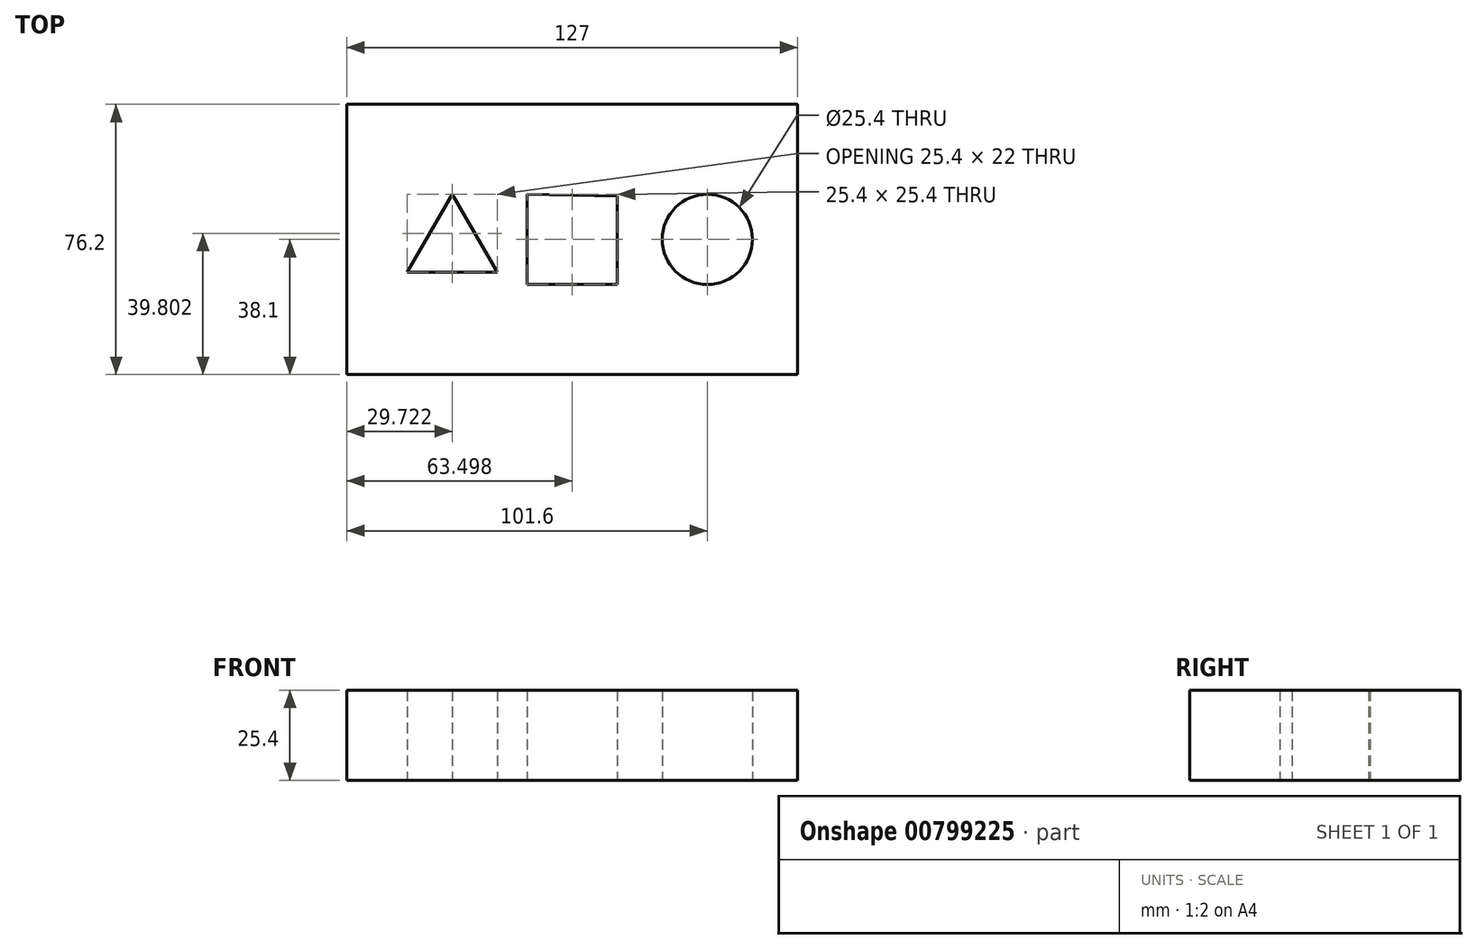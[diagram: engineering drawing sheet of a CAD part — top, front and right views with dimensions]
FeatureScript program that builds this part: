
annotation { "Feature Type Name" : "Feature", "Feature Type Description" : "" }
export const myFeature = defineFeature(function(context is Context, id is Id, definition is map)
    precondition{}
    {
        {
            var Q0;
            Q0=qCreatedBy(makeId("Top.planeOp"),FACE);
            var sketch = newSketch(context, id + "F0", { "sketchPlane" : qUnion([Q0])});
            skLineSegment(sketch, "E0.bottom", {"start": v(63.5, 38.1) * mm, "end": v(-63.5, 38.1) * mm});
            skLineSegment(sketch, "E0.top", {"start": v(63.5, -38.1) * mm, "end": v(-63.5, -38.1) * mm});
            skLineSegment(sketch, "E0.left", {"start": v(63.5, 38.1) * mm, "end": v(63.5, -38.1) * mm});
            skLineSegment(sketch, "E0.right", {"start": v(-63.5, 38.1) * mm, "end": v(-63.5, -38.1) * mm});
            skPoint(sketch, "E0.middle", {"position": v(0, 0) * mm});
            skLineSegment(sketch, "E1", {"start": v(-33.78, 12.7) * mm, "end": v(-46.48, -9.3) * mm});
            skLineSegment(sketch, "E2", {"start": v(-46.48, -9.3) * mm, "end": v(-21.08, -9.3) * mm});
            skLineSegment(sketch, "E3", {"start": v(-21.08, -9.3) * mm, "end": v(-33.78, 12.7) * mm});
            skLineSegment(sketch, "E4", {"start": v(-12.7, 12.7) * mm, "end": v(-12.7, -12.7) * mm});
            skLineSegment(sketch, "E5", {"start": v(-12.7, -12.7) * mm, "end": v(12.7, -12.7) * mm});
            skLineSegment(sketch, "E6", {"start": v(12.7, -12.7) * mm, "end": v(12.7, 12.26) * mm});
            skLineSegment(sketch, "E7", {"start": v(12.7, 12.26) * mm, "end": v(-12.7, 12.7) * mm});
            skCircle(sketch, "E8", {"center": v(38.1, 0) * mm, "radius": 12.7 * mm});
            skSolve(sketch);
        }
        {
            var Q0;
            Q0=makeQuery(id+"F0.imprint","IMPRINT",FACE,{"disambiguationData":[TD([[makeQuery(id+"F0.imprint","IMPRINT",EDGE,{"derivedFrom":sQuery(id+"F0.wireOp",EDGE,"E0.bottom")}),1.0]])]});
            extrude(context, id + "F1", {"entities" : qUnion([Q0]), "depth" : 25.4 * mm, "offsetDistance" : 25.4 * mm});
        }
    });
